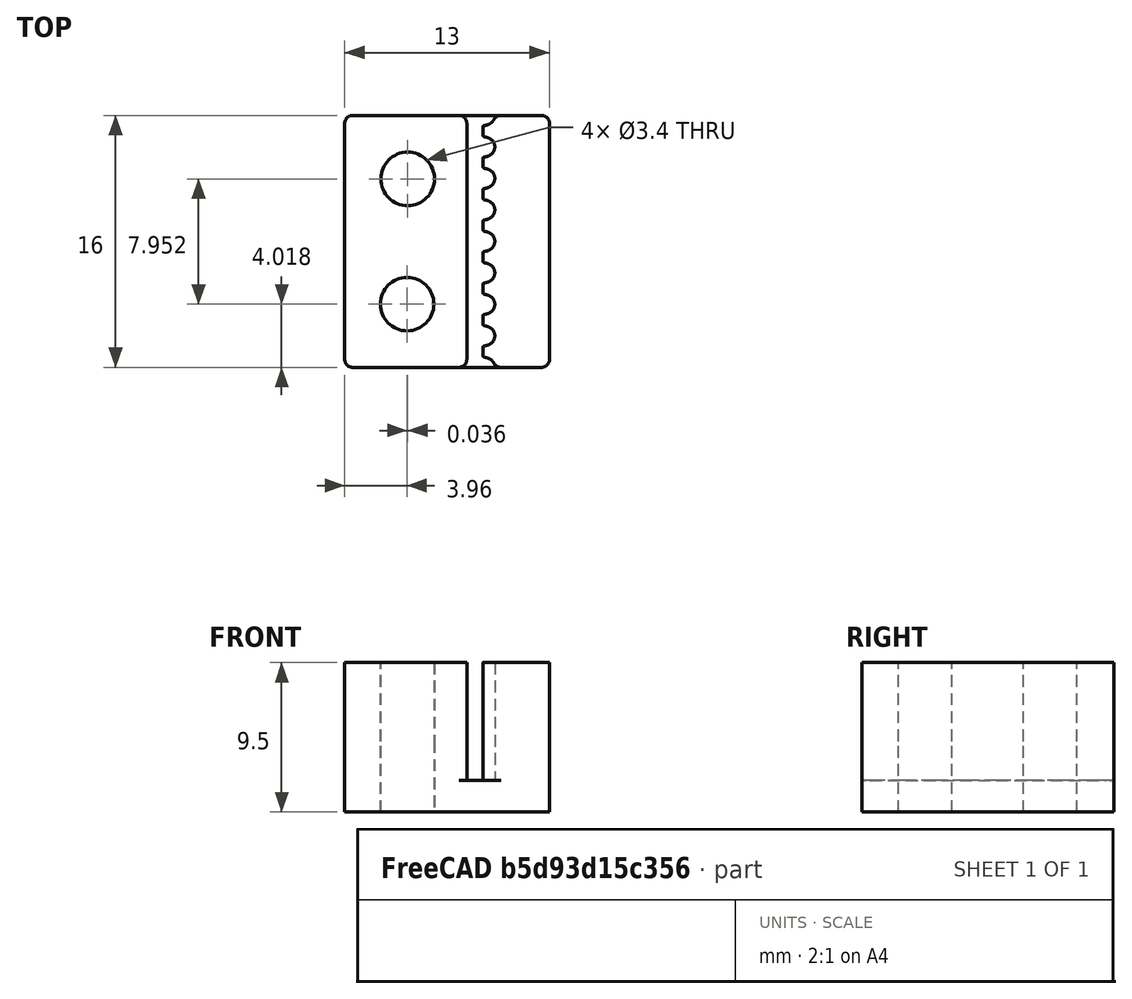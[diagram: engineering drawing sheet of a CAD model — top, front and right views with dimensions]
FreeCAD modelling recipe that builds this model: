
FCSTD DOCUMENT  (FreeCAD 0.18.4R)
Label: belt_clamp_general
License: All rights reserved
LicenseURL: http://en.wikipedia.org/wiki/All_rights_reserved
objects: PartDesign::Pocket×2, Part::Feature×1, PartDesign::FeatureBase×1, Sketcher::SketchObject×1, PartDesign::Body×1
note: 8 computed .brp shape members not serialized (recipe doc carries the construction recipe); baked Part::Feature solids carry a one-line shape summary decoded from their .brp

FEATURE [Part::Feature] Part__Feature  label="FusionComponent"
  shape: bbox 13 x 16 x 9.5 mm, 68 faces (baked)
FEATURE [PartDesign::FeatureBase] BaseFeature
  BaseFeature = -> Part__Feature
FEATURE [Sketcher::SketchObject] Sketch
  MapMode = 5
  Placement = pos=(0,0,9.5) rot=(0,0,1;0rad)
  Support = -> [BaseFeature]
  sketch-geometry (2):
    g0: Circle CenterX=3.9957 CenterY=11.9699 CenterZ=0 NormalX=0 NormalY=0 NormalZ=1 AngleXU=0 Radius=1.7
    g1: Circle CenterX=3.95985 CenterY=4.01794 CenterZ=0 NormalX=0 NormalY=0 NormalZ=1 AngleXU=0 Radius=1.7
  constraints (2):
    c: Radius(g0) = 1.7
    c: Radius(g1) = 1.7
FEATURE [PartDesign::Pocket] Pocket
  BaseFeature = -> BaseFeature
  Length = 10
  Length2 = 100
  Profile = -> Sketch
  Type = 0
FEATURE [PartDesign::Pocket] Pocket001
  BaseFeature = -> Pocket
  Length = 5
  Length2 = 100
  Profile = -> Sketch
  Type = 0
FEATURE [PartDesign::Body] Body
  BaseFeature = -> Part__Feature
  Group = -> [BaseFeature,Sketch,Pocket,Pocket001]
  Origin = -> Origin
  Tip = -> Pocket001
